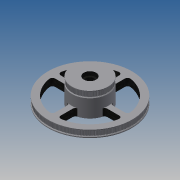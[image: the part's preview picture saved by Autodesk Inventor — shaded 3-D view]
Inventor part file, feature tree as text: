
AUTODESK INVENTOR PART (.ipt)
format: ipt  version: 2013 (Build 170138000, 138)  size: 1,575,936 bytes
history: native  units: mm
features: extrude x5, sketch x5, other x3, fillet x1, pattern_circular x1, projected_geometry x1
ambient origin geometry x8: Origin, YZ Plane, XZ Plane, XY Plane, X Axis, Y Axis, Z Axis, Center Point
bodies: Solid1 (feature_tree)
feature tree (16):
  other  "distal idler pulley.iam"
  other  "235 pulley blank.ipt:1"
  other  "100 pulley blank.ipt:1"
  extrude  "Extrusion1"  Depth=10.0mm TaperAngle=0.0deg
  extrude  "Extrusion2"  Depth=5.0mm
  fillet  "Fillet1"  [1 undecoded]
  pattern_circular  "Circular Pattern1"  Count=4 Angle=360.0deg
  extrude  "Extrusion3"  Depth=15.0mm
  extrude  "Extrusion4"  Depth=10.0mm TaperAngle=0.0deg
  extrude  "Extrusion5"  Depth=22.0mm
  sketch  "Sketch1"  dims[d0=10.0mm d1=10.0mm d2=0.0mm]
  projected_geometry  "Projected Loop1"
  sketch  "Sketch2"  dims[d3=5.0mm d4=5.0mm d5=0.0mm]
  sketch  "Sketch3"  dims[d6=12.0mm]
  sketch  "Sketch4"  dims[d7=10.0mm d8=0.0mm]
  sketch  "Sketch5"  dims[d9=5.0mm d10=40.0mm d11=360.0deg d13=15.0mm d15=10.0mm d16=0.0mm d17=22.0mm d19=7.0mm d20=0.0mm d21=22.0mm d23=7.0mm d24=0.0mm]
note: 1 required parameter value undecoded (feature->parameter linkage not recoverable at this tier; creation-order binding heuristic only, values carry confidence <= 0.55)
